SOLIDWORKS PART (.sldprt)
format: sldprt  version: not decoded by parser v0  size: 254,464 bytes
history: native  units: mm
features: sketch x8, cut_extrude x5, plane x3, extrude x3, material x1, fillet x1 (+10 scaffold rows collapsed)
feature tree (31):
  scaffold x10  (default folders/planes/origin — collapsed)
  material  "Matériau <non spécifié>"
  plane  "Plan de face"
  plane  "Plan de dessus"
  plane  "Plan de droite"
  sketch  "Esquisse1"  dims[D1=1.65mm D2=1.9mm]
  extrude  "Extrusion1"  Depth=15.8mm
  sketch  "Esquisse2"  dims[D1=~9.254537mm]
  cut_extrude  "Enlèv. mat.-Extru.1"  Depth=1mm
  sketch  "Esquisse3"  dims[D1=~10.595727mm]
  cut_extrude  "Enlèv. mat.-Extru.2"  Depth=1mm
  sketch  "Esquisse4"  dims[D1=~10.180081mm]
  cut_extrude  "Enlèv. mat.-Extru.3"  Depth=1mm
  sketch  "Esquisse6"  dims[D1=~9.158541mm]
  cut_extrude  "Enlèv. mat.-Extru.4"  Depth=1mm
  sketch  "Esquisse7"  dims[D1=~4.576702mm]
  extrude  "Extrusion3"  Depth=5mm
  sketch  "Esquisse8"  dims[D1=~4.087826mm]
  extrude  "Extrusion4"  Depth=1mm
  sketch  "Esquisse9"  dims[D1=~1.13238mm]
  cut_extrude  "Enlèv. mat.-Extru.5"  [1 undecoded]
  fillet  "Congé1"  Radius=6.5mm
decode coverage: 16 of 17 modeling features carry decoded parameters
note: ~ marks probable driven/reference dimensions
note: 1 parameter value undecoded
note: suppression state not decoded; provenance and decode notes live in map.json
